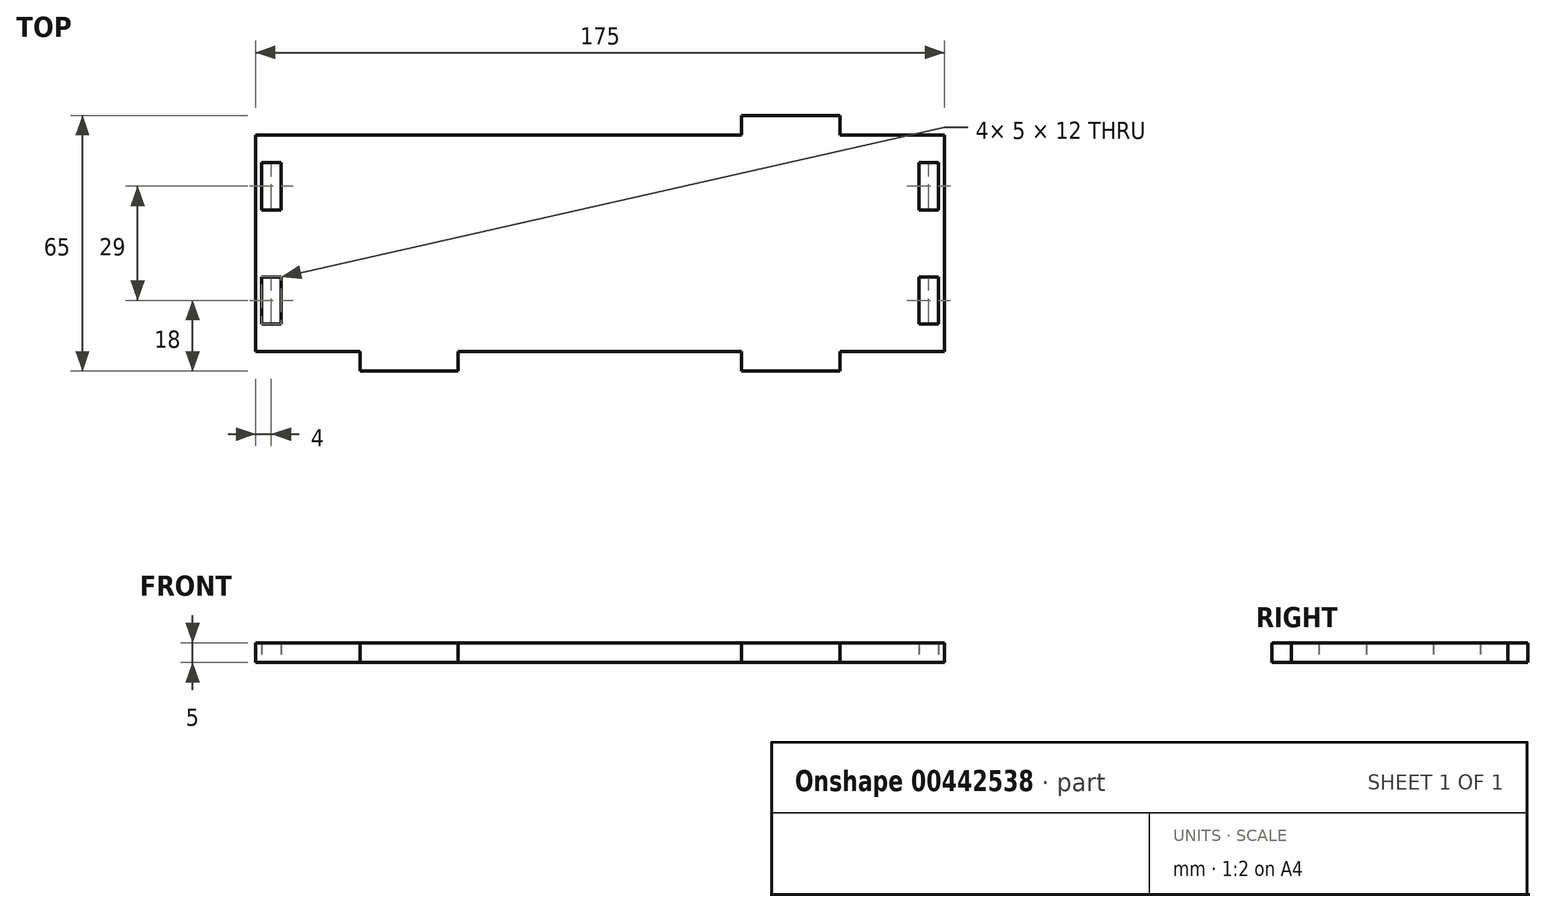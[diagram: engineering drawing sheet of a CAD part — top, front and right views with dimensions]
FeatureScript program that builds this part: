
annotation { "Feature Type Name" : "Feature", "Feature Type Description" : "" }
export const myFeature = defineFeature(function(context is Context, id is Id, definition is map)
    precondition{}
    {
        {
            var Q0;
            Q0=qCreatedBy(makeId("Top.planeOp"),FACE);
            var sketch = newSketch(context, id + "F0", { "sketchPlane" : qUnion([Q0])});
            skLineSegment(sketch, "E0.bottom", {"start": v(87.5, 27.5) * mm, "end": v(-87.5, 27.5) * mm});
            skLineSegment(sketch, "E0.top", {"start": v(87.5, -27.5) * mm, "end": v(-87.5, -27.5) * mm});
            skLineSegment(sketch, "E0.left", {"start": v(87.5, 27.5) * mm, "end": v(87.5, -27.5) * mm});
            skLineSegment(sketch, "E0.right", {"start": v(-87.5, 27.5) * mm, "end": v(-87.5, -27.5) * mm});
            skPoint(sketch, "E0.middle", {"position": v(0, 0) * mm});
            skLineSegment(sketch, "E1.bottom", {"start": v(-61, 27.5) * mm, "end": v(-36, 27.5) * mm});
            skLineSegment(sketch, "E1.top", {"start": v(-61, 32.5) * mm, "end": v(-36, 32.5) * mm});
            skLineSegment(sketch, "E1.left", {"start": v(-61, 27.5) * mm, "end": v(-61, 32.5) * mm});
            skLineSegment(sketch, "E1.right", {"start": v(-36, 27.5) * mm, "end": v(-36, 32.5) * mm});
            skLineSegment(sketch, "E2.bottom", {"start": v(-86, 20.5) * mm, "end": v(-81, 20.5) * mm});
            skLineSegment(sketch, "E2.top", {"start": v(-86, 8.5) * mm, "end": v(-81, 8.5) * mm});
            skLineSegment(sketch, "E2.left", {"start": v(-86, 20.5) * mm, "end": v(-86, 8.5) * mm});
            skLineSegment(sketch, "E2.right", {"start": v(-81, 20.5) * mm, "end": v(-81, 8.5) * mm});
            skLineSegment(sketch, "E3", {"start": v(0, 27.5) * mm, "end": v(0, -27.5) * mm, "construction": true});
            skLineSegment(sketch, "E4", {"start": v(-87.5, 0) * mm, "end": v(87.5, 0) * mm, "construction": true});
            skLineSegment(sketch, "E5.MirrorCS", {"start": v(-86, -20.5) * mm, "end": v(-81, -20.5) * mm});
            skLineSegment(sketch, "E6.MirrorCS", {"start": v(-86, -20.5) * mm, "end": v(-86, -8.5) * mm});
            skLineSegment(sketch, "E7.MirrorCS", {"start": v(-86, -8.5) * mm, "end": v(-81, -8.5) * mm});
            skLineSegment(sketch, "E8.MirrorCS", {"start": v(-81, -20.5) * mm, "end": v(-81, -8.5) * mm});
            skLineSegment(sketch, "E9.MirrorCS", {"start": v(-61, -32.5) * mm, "end": v(-36, -32.5) * mm});
            skLineSegment(sketch, "E10.MirrorCS", {"start": v(-36, -27.5) * mm, "end": v(-36, -32.5) * mm});
            skLineSegment(sketch, "E11.MirrorCS", {"start": v(-61, -27.5) * mm, "end": v(-61, -32.5) * mm});
            skLineSegment(sketch, "E12.MirrorCS", {"start": v(86, -8.5) * mm, "end": v(81, -8.5) * mm});
            skLineSegment(sketch, "E13.MirrorCS", {"start": v(61, -32.5) * mm, "end": v(36, -32.5) * mm});
            skLineSegment(sketch, "E14.MirrorCS", {"start": v(61, -27.5) * mm, "end": v(61, -32.5) * mm});
            skLineSegment(sketch, "E15.MirrorCS", {"start": v(36, 27.5) * mm, "end": v(36, 32.5) * mm});
            skLineSegment(sketch, "E16.MirrorCS", {"start": v(86, 8.5) * mm, "end": v(81, 8.5) * mm});
            skLineSegment(sketch, "E17.MirrorCS", {"start": v(36, -27.5) * mm, "end": v(36, -32.5) * mm});
            skLineSegment(sketch, "E18.MirrorCS", {"start": v(86, 20.5) * mm, "end": v(86, 8.5) * mm});
            skLineSegment(sketch, "E19.MirrorCS", {"start": v(86, 20.5) * mm, "end": v(81, 20.5) * mm});
            skLineSegment(sketch, "E20.MirrorCS", {"start": v(81, -20.5) * mm, "end": v(81, -8.5) * mm});
            skLineSegment(sketch, "E21.MirrorCS", {"start": v(86, -20.5) * mm, "end": v(81, -20.5) * mm});
            skLineSegment(sketch, "E22.MirrorCS", {"start": v(86, -20.5) * mm, "end": v(86, -8.5) * mm});
            skLineSegment(sketch, "E23.MirrorCS", {"start": v(61, 27.5) * mm, "end": v(61, 32.5) * mm});
            skLineSegment(sketch, "E24.MirrorCS", {"start": v(81, 20.5) * mm, "end": v(81, 8.5) * mm});
            skLineSegment(sketch, "E25.MirrorCS", {"start": v(61, 32.5) * mm, "end": v(36, 32.5) * mm});
            skLineSegment(sketch, "E26.MirrorCS", {"start": v(61, 27.5) * mm, "end": v(36, 27.5) * mm});
            skSolve(sketch);
        }
        {
            var Q0;
            {var subQ3=sQuery(id+"F0.wireOp",EDGE,"E0.right");Q0=makeQuery(id+"F0.imprint","IMPRINT",FACE,{"disambiguationData":[TD([[makeQuery(id+"F0.imprint","IMPRINT",EDGE,{"derivedFrom":subQ3}),1.0]])]});}
            var Q1;
            Q1=makeQuery(id+"F0.imprint","IMPRINT",FACE,{"disambiguationData":[TD([[makeQuery(id+"F0.imprint","IMPRINT",EDGE,{"derivedFrom":sQuery(id+"F0.wireOp",EDGE,"E1.bottom")}),1.0]])]});
            var Q2;
            Q2=makeQuery(id+"F0.imprint","IMPRINT",FACE,{"disambiguationData":[TD([[makeQuery(id+"F0.imprint","IMPRINT",EDGE,{"derivedFrom":sQuery(id+"F0.wireOp",EDGE,"E15.MirrorCS")}),-1.0]])]});
            var Q3;
            Q3=makeQuery(id+"F0.imprint","IMPRINT",FACE,{"disambiguationData":[TD([[makeQuery(id+"F0.imprint","IMPRINT",EDGE,{"derivedFrom":sQuery(id+"F0.wireOp",EDGE,"E13.MirrorCS")}),-1.0]])]});
            var Q4;
            Q4=makeQuery(id+"F0.imprint","IMPRINT",FACE,{"disambiguationData":[TD([[makeQuery(id+"F0.imprint","IMPRINT",EDGE,{"derivedFrom":sQuery(id+"F0.wireOp",EDGE,"E9.MirrorCS")}),1.0]])]});
            extrude(context, id + "F1", {"entities" : qUnion([Q0, Q1, Q2, Q3, Q4]), "depth" : 5 * mm});
        }
    });
